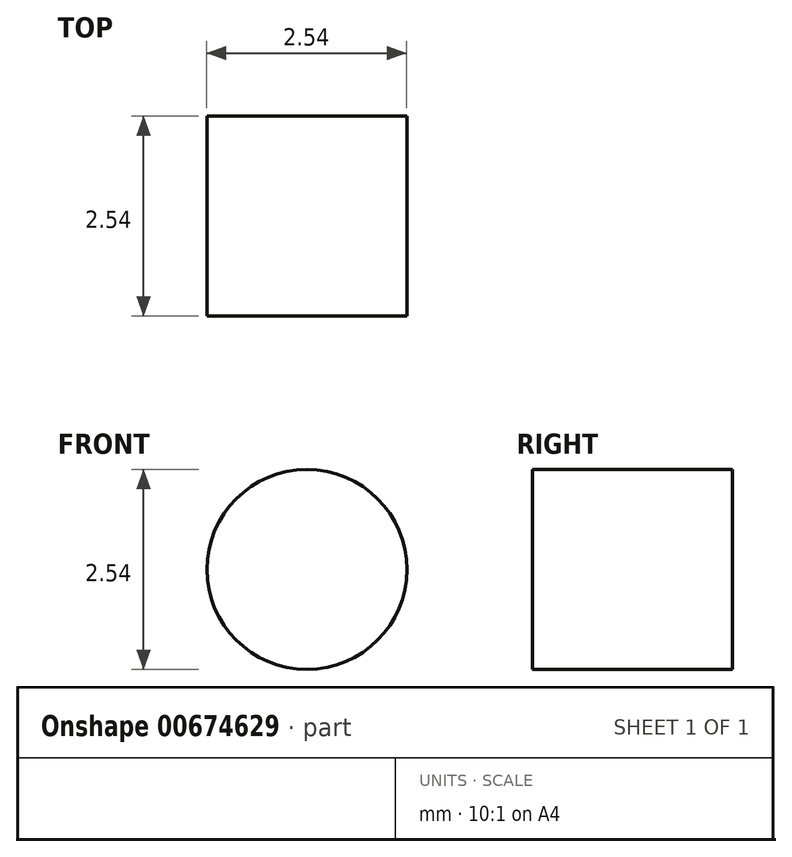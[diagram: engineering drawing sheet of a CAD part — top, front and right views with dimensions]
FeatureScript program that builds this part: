
annotation { "Feature Type Name" : "Feature", "Feature Type Description" : "" }
export const myFeature = defineFeature(function(context is Context, id is Id, definition is map)
    precondition{}
    {
        {
            var Q0;
            Q0=qCreatedBy(makeId("Front.planeOp"),FACE);
            var sketch = newSketch(context, id + "F0", { "sketchPlane" : qUnion([Q0])});
            skLineSegment(sketch, "E0.bottom", {"start": v(-31.4, -74.12) * mm, "end": v(31.4, -74.12) * mm});
            skLineSegment(sketch, "E0.top", {"start": v(-31.4, 74.12) * mm, "end": v(31.4, 74.12) * mm});
            skLineSegment(sketch, "E0.left", {"start": v(-37.75, -67.77) * mm, "end": v(-37.75, 67.77) * mm});
            skLineSegment(sketch, "E0.right", {"start": v(37.75, -67.77) * mm, "end": v(37.75, 67.77) * mm});
            skPoint(sketch, "E0.middle", {"position": v(0, 0) * mm});
            skPoint(sketch, "E1.visualSharp", {"position": v(-37.75, 74.12) * mm});
            skArc(sketch, "E1.filletArc", {"start": v(-31.4, 74.12) * mm, "mid": v(-35.9, 72.27) * mm, "end": v(-37.75, 67.77) * mm});
            skPoint(sketch, "E2.visualSharp", {"position": v(37.75, 74.12) * mm});
            skArc(sketch, "E2.filletArc", {"start": v(37.75, 67.77) * mm, "mid": v(35.9, 72.27) * mm, "end": v(31.4, 74.12) * mm});
            skPoint(sketch, "E3.visualSharp", {"position": v(37.75, -74.12) * mm});
            skArc(sketch, "E3.filletArc", {"start": v(31.4, -74.12) * mm, "mid": v(35.9, -72.27) * mm, "end": v(37.75, -67.77) * mm});
            skPoint(sketch, "E4.visualSharp", {"position": v(-37.75, -74.12) * mm});
            skArc(sketch, "E4.filletArc", {"start": v(-37.75, -67.77) * mm, "mid": v(-35.9, -72.27) * mm, "end": v(-31.4, -74.12) * mm});
            skLineSegment(sketch, "E5", {"start": v(37.75, 67.77) * mm, "end": v(-37.75, 67.77) * mm});
            skLineSegment(sketch, "E6", {"start": v(37.75, -61.42) * mm, "end": v(-37.75, -61.42) * mm});
            skLineSegment(sketch, "E7", {"start": v(31.4, -67.77) * mm, "end": v(-31.4, -67.77) * mm});
            skCircle(sketch, "E8", {"center": v(0, -67.77) * mm, "radius": 5.72 * mm});
            skLineSegment(sketch, "E9", {"start": v(31.4, 74.12) * mm, "end": v(31.4, 67.77) * mm});
            skLineSegment(sketch, "E10", {"start": v(31.4, 70.95) * mm, "end": v(-31.75, 70.95) * mm});
            skLineSegment(sketch, "E11", {"start": v(0, 74.12) * mm, "end": v(0, 67.77) * mm});
            skLineSegment(sketch, "E12", {"start": v(-31.4, 74.12) * mm, "end": v(0, 67.77) * mm});
            skLineSegment(sketch, "E13", {"start": v(0, 67.77) * mm, "end": v(31.4, 74.12) * mm});
            skCircle(sketch, "E14", {"center": v(-0.18, 70.95) * mm, "radius": 1.27 * mm});
            skSolve(sketch);
        }
        {
            var Q0;
            {var subQ0=sQuery(id+"F0.wireOp",EDGE,"E11");var subQ1=sQuery(id+"F0.wireOp",EDGE,"E10");var subQ2=makeQuery(id+"F0.imprint","INTERSECT",VERTEX,{"derivedFrom":[subQ1,subQ0]});Q0=makeQuery(id+"F0.imprint","IMPRINT",FACE,{"disambiguationData":[TD([[makeQuery(id+"F0.imprint","IMPRINT",EDGE,{"disambiguationData":[TD([[subQ2,-1.0]])],"derivedFrom":subQ1}),-1.0]])]});}
            var Q1;
            {var subQ0=sQuery(id+"F0.wireOp",EDGE,"E14");var subQ1=sQuery(id+"F0.wireOp",EDGE,"E10");var subQ2=makeQuery(id+"F0.imprint","INTERSECT",VERTEX,{"disambiguationData":[OD(0.0)],"derivedFrom":[subQ1,subQ0]});Q1=makeQuery(id+"F0.imprint","IMPRINT",FACE,{"disambiguationData":[TD([[makeQuery(id+"F0.imprint","IMPRINT",EDGE,{"disambiguationData":[TD([[subQ2,-1.0]])],"derivedFrom":subQ1}),-1.0]])]});}
            var Q2;
            {var subQ0=sQuery(id+"F0.wireOp",EDGE,"E14");var subQ1=sQuery(id+"F0.wireOp",EDGE,"E10");var subQ2=makeQuery(id+"F0.imprint","INTERSECT",VERTEX,{"disambiguationData":[OD(0.0)],"derivedFrom":[subQ1,subQ0]});Q2=makeQuery(id+"F0.imprint","IMPRINT",FACE,{"disambiguationData":[TD([[makeQuery(id+"F0.imprint","IMPRINT",EDGE,{"disambiguationData":[TD([[subQ2,-1.0]])],"derivedFrom":subQ1}),1.0]])]});}
            var Q3;
            {var subQ0=sQuery(id+"F0.wireOp",EDGE,"E11");var subQ1=sQuery(id+"F0.wireOp",EDGE,"E10");var subQ2=makeQuery(id+"F0.imprint","INTERSECT",VERTEX,{"derivedFrom":[subQ1,subQ0]});Q3=makeQuery(id+"F0.imprint","IMPRINT",FACE,{"disambiguationData":[TD([[makeQuery(id+"F0.imprint","IMPRINT",EDGE,{"disambiguationData":[TD([[subQ2,-1.0]])],"derivedFrom":subQ1}),1.0]])]});}
            extrude(context, id + "F1", {"entities" : qUnion([Q0, Q1, Q2, Q3]), "oppositeDirection" : true, "depth" : 2.54 * mm, "offsetDistance" : 25.4 * mm});
        }
    });
